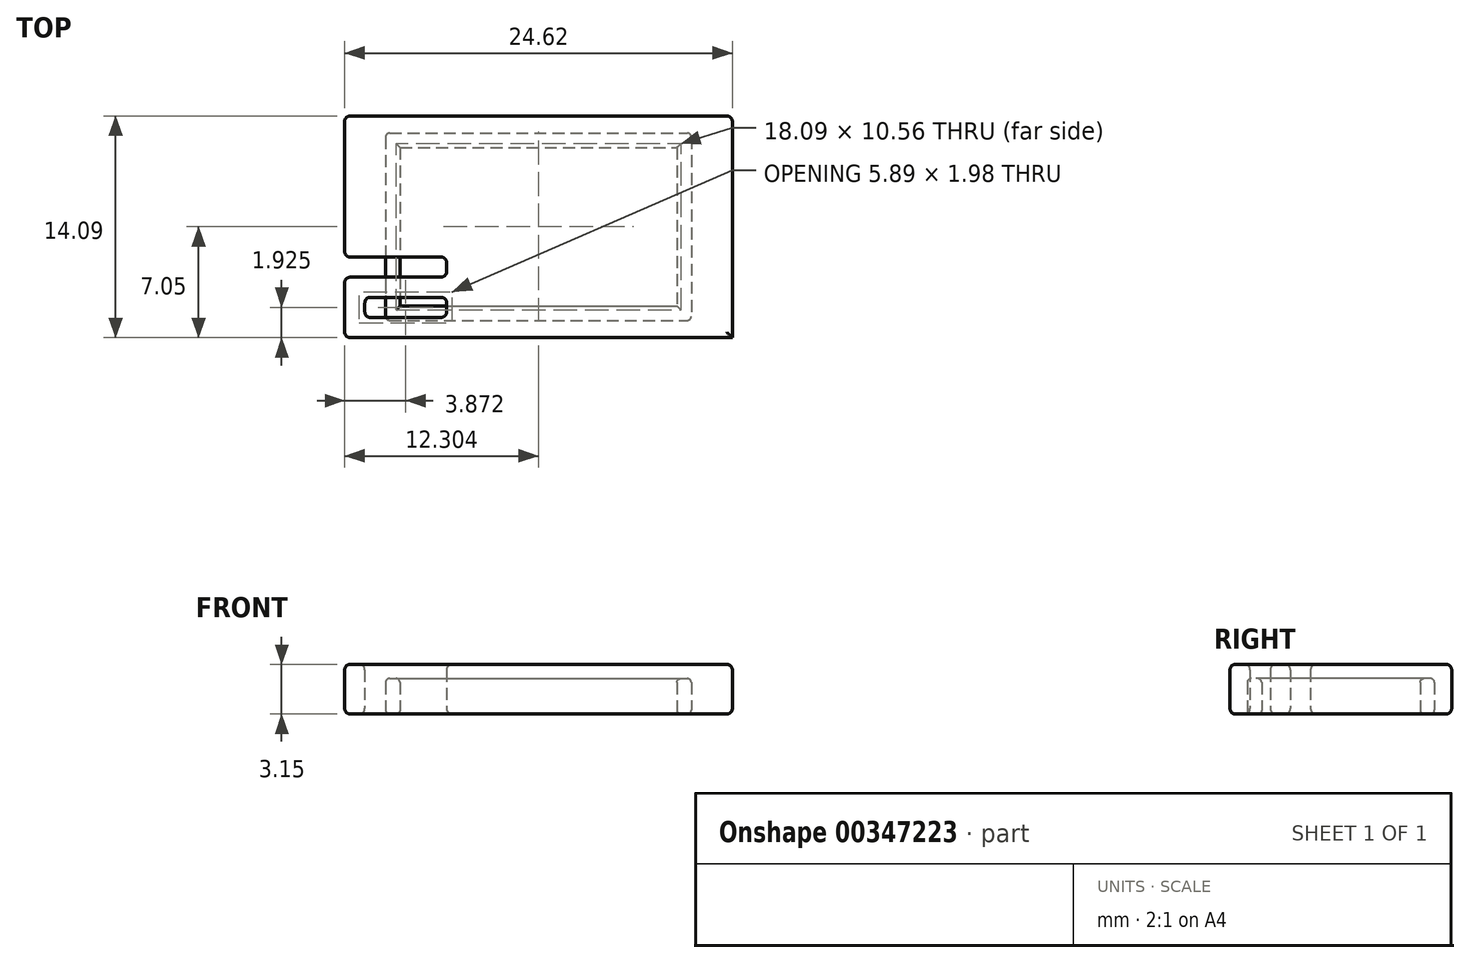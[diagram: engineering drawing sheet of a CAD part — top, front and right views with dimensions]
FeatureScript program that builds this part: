
annotation { "Feature Type Name" : "Feature", "Feature Type Description" : "" }
export const myFeature = defineFeature(function(context is Context, id is Id, definition is map)
    precondition{}
    {
        {
            var Q0;
            Q0=qCreatedBy(makeId("Top.planeOp"),FACE);
            var sketch = newSketch(context, id + "F0", { "sketchPlane" : qUnion([Q0])});
            skPoint(sketch, "E0.middle", {"position": v(0, 0) * mm});
            skLineSegment(sketch, "E1.bottom", {"start": v(-8.79, 5.02) * mm, "end": v(8.8, 5.02) * mm});
            skLineSegment(sketch, "E1.top", {"start": v(-8.79, -5.04) * mm, "end": v(-3.25, -5.04) * mm});
            skLineSegment(sketch, "E1.left", {"start": v(-8.79, 5.02) * mm, "end": v(-8.79, -5.04) * mm});
            skLineSegment(sketch, "E1.right", {"start": v(8.8, 5.02) * mm, "end": v(8.8, -5.04) * mm});
            skLineSegment(sketch, "E2", {"start": v(-8.79, 0.45) * mm, "end": v(-3.25, 0.45) * mm});
            skLineSegment(sketch, "E3", {"start": v(-3.25, 0.45) * mm, "end": v(-3.25, 1.36) * mm});
            skLineSegment(sketch, "E4", {"start": v(-3.25, 1.36) * mm, "end": v(-7.87, 1.36) * mm});
            skLineSegment(sketch, "E5", {"start": v(-3.25, 2.73) * mm, "end": v(-4.32, 2.73) * mm, "construction": true});
            skLineSegment(sketch, "E6.MirrorCS", {"start": v(-3.25, 4.1) * mm, "end": v(-7.87, 4.1) * mm});
            skLineSegment(sketch, "E7", {"start": v(-7.87, 4.1) * mm, "end": v(-7.87, 1.36) * mm});
            skLineSegment(sketch, "E8", {"start": v(-2.54, 0.45) * mm, "end": v(-2.54, 5.02) * mm});
            skLineSegment(sketch, "E9", {"start": v(-2.54, 0.45) * mm, "end": v(-1.62, 0.45) * mm});
            skLineSegment(sketch, "E10.trimOffspring", {"start": v(-3.25, 4.1) * mm, "end": v(-3.25, 5.02) * mm});
            skLineSegment(sketch, "E11", {"start": v(-1.62, 4.1) * mm, "end": v(-1.62, 0.45) * mm});
            skLineSegment(sketch, "E12", {"start": v(8.8, 0.45) * mm, "end": v(3.26, 0.45) * mm});
            skLineSegment(sketch, "E13.0", {"start": v(8.8, 1.36) * mm, "end": v(3.27, 1.36) * mm});
            skLineSegment(sketch, "E14.0", {"start": v(8.8, 2.28) * mm, "end": v(3.26, 2.28) * mm});
            skLineSegment(sketch, "E15.0", {"start": v(8.8, 3.2) * mm, "end": v(3.27, 3.2) * mm});
            skLineSegment(sketch, "E16.0", {"start": v(8.8, 4.1) * mm, "end": v(3.26, 4.1) * mm});
            skLineSegment(sketch, "E17", {"start": v(3.26, 0.45) * mm, "end": v(3.27, 1.36) * mm});
            skLineSegment(sketch, "E18", {"start": v(3.26, 2.28) * mm, "end": v(3.27, 3.2) * mm});
            skLineSegment(sketch, "E19", {"start": v(3.26, 4.1) * mm, "end": v(3.26, 5.02) * mm});
            skLineSegment(sketch, "E20", {"start": v(-1.62, 4.1) * mm, "end": v(2.5, 4.1) * mm});
            skLineSegment(sketch, "E21", {"start": v(2.5, 4.1) * mm, "end": v(2.5, 5.02) * mm});
            skLineSegment(sketch, "E22", {"start": v(-8.79, -0.47) * mm, "end": v(-3.25, -0.47) * mm});
            skLineSegment(sketch, "E23", {"start": v(3.26, -0.47) * mm, "end": v(3.26, -1.38) * mm});
            skLineSegment(sketch, "E24.0", {"start": v(-7.87, -4.13) * mm, "end": v(-4.17, -4.13) * mm});
            skLineSegment(sketch, "E25.0", {"start": v(-7.87, -3.21) * mm, "end": v(-4.17, -3.21) * mm});
            skLineSegment(sketch, "E26.0", {"start": v(-8.79, -2.3) * mm, "end": v(-4.17, -2.3) * mm});
            skLineSegment(sketch, "E27.0", {"start": v(-8.79, -1.38) * mm, "end": v(-4.17, -1.38) * mm});
            skLineSegment(sketch, "E28", {"start": v(2.5, -0.47) * mm, "end": v(2.5, -1.38) * mm});
            skLineSegment(sketch, "E29", {"start": v(-2.54, -0.47) * mm, "end": v(-2.54, -1.38) * mm});
            skLineSegment(sketch, "E30", {"start": v(-0.46, -1.38) * mm, "end": v(-0.46, -5.04) * mm});
            skLineSegment(sketch, "E31.0", {"start": v(0.45, -1.38) * mm, "end": v(0.45, -5.04) * mm});
            skLineSegment(sketch, "E32.trimOffspring", {"start": v(0.45, -1.38) * mm, "end": v(2.5, -1.38) * mm});
            skLineSegment(sketch, "E33.trimOffspring", {"start": v(3.26, -2.3) * mm, "end": v(8.8, -2.3) * mm});
            skLineSegment(sketch, "E34.trimOffspring", {"start": v(3.26, -4.13) * mm, "end": v(8.8, -4.13) * mm});
            skLineSegment(sketch, "E35", {"start": v(-3.25, -0.47) * mm, "end": v(-3.25, -5.04) * mm});
            skLineSegment(sketch, "E36", {"start": v(-4.17, -1.38) * mm, "end": v(-4.17, -2.3) * mm});
            skLineSegment(sketch, "E37", {"start": v(-4.17, -3.21) * mm, "end": v(-4.17, -4.13) * mm});
            skLineSegment(sketch, "E38", {"start": v(-7.87, -3.21) * mm, "end": v(-7.87, -4.13) * mm});
            skLineSegment(sketch, "E39.trimOffspring", {"start": v(-2.54, -1.38) * mm, "end": v(-0.46, -1.38) * mm});
            skLineSegment(sketch, "E40.0", {"start": v(-9.7, 5.93) * mm, "end": v(9.71, 5.93) * mm});
            skLineSegment(sketch, "E40.1", {"start": v(-9.7, 5.93) * mm, "end": v(-9.7, -5.95) * mm});
            skLineSegment(sketch, "E40.2", {"start": v(-9.7, -5.95) * mm, "end": v(9.71, -5.95) * mm});
            skLineSegment(sketch, "E40.3", {"start": v(9.71, 5.93) * mm, "end": v(9.71, -5.95) * mm});
            skLineSegment(sketch, "E41.trimOffspring", {"start": v(3.26, -3.21) * mm, "end": v(8.8, -3.21) * mm});
            skLineSegment(sketch, "E42.trimOffspring", {"start": v(3.26, -5.04) * mm, "end": v(8.8, -5.04) * mm});
            skLineSegment(sketch, "E43.trimOffspring", {"start": v(-0.46, -5.04) * mm, "end": v(0.45, -5.04) * mm});
            skLineSegment(sketch, "E44.trimOffspring", {"start": v(-2.54, -0.47) * mm, "end": v(2.5, -0.47) * mm});
            skLineSegment(sketch, "E45.trimOffspring", {"start": v(3.26, -0.47) * mm, "end": v(8.8, -0.47) * mm});
            skLineSegment(sketch, "E46.trimOffspring", {"start": v(3.26, -1.38) * mm, "end": v(8.8, -1.38) * mm});
            skLineSegment(sketch, "E47.trimOffspring", {"start": v(3.26, -2.3) * mm, "end": v(3.26, -3.21) * mm});
            skLineSegment(sketch, "E48.trimOffspring", {"start": v(3.26, -4.13) * mm, "end": v(3.26, -5.04) * mm});
            skLineSegment(sketch, "E49.top", {"start": v(-8.79, -5.04) * mm, "end": v(8.8, -5.04) * mm});
            skSolve(sketch);
        }
        {
            var Q0;
            {var subQ0=sQuery(id+"F0.wireOp",EDGE,"E2");Q0=makeQuery(id+"F0.imprint","IMPRINT",FACE,{"disambiguationData":[TD([[makeQuery(id+"F0.imprint","IMPRINT",EDGE,{"derivedFrom":subQ0}),1.0]])]});}
            var Q1;
            {var subQ0=sQuery(id+"F0.wireOp",EDGE,"E8");Q1=makeQuery(id+"F0.imprint","IMPRINT",FACE,{"disambiguationData":[TD([[makeQuery(id+"F0.imprint","IMPRINT",EDGE,{"derivedFrom":subQ0}),-1.0]])]});}
            var Q2;
            {var subQ3=sQuery(id+"F0.wireOp",EDGE,"E19");Q2=makeQuery(id+"F0.imprint","IMPRINT",FACE,{"disambiguationData":[TD([[makeQuery(id+"F0.imprint","IMPRINT",EDGE,{"derivedFrom":subQ3}),-1.0]])]});}
            var Q3;
            {var subQ5=sQuery(id+"F0.wireOp",EDGE,"E18");Q3=makeQuery(id+"F0.imprint","IMPRINT",FACE,{"disambiguationData":[TD([[makeQuery(id+"F0.imprint","IMPRINT",EDGE,{"derivedFrom":subQ5}),-1.0]])]});}
            var Q4;
            {var subQ0=sQuery(id+"F0.wireOp",EDGE,"E12");Q4=makeQuery(id+"F0.imprint","IMPRINT",FACE,{"disambiguationData":[TD([[makeQuery(id+"F0.imprint","IMPRINT",EDGE,{"derivedFrom":subQ0}),-1.0]])]});}
            var Q5;
            {var subQ0=sQuery(id+"F0.wireOp",EDGE,"E22");var subQ1=sQuery(id+"F0.wireOp",EDGE,"E1.right");var subQ2=makeQuery(id+"F0.imprint","INTERSECT",VERTEX,{"derivedFrom":[subQ1,subQ0]});Q5=makeQuery(id+"F0.imprint","IMPRINT",FACE,{"disambiguationData":[TD([[makeQuery(id+"F0.imprint","IMPRINT",EDGE,{"disambiguationData":[TD([[subQ2,-1.0]])],"derivedFrom":subQ1}),-1.0]])]});}
            var Q6;
            {var subQ0=sQuery(id+"F0.wireOp",EDGE,"E33.trimOffspring");var subQ1=sQuery(id+"F0.wireOp",EDGE,"E1.right");var subQ2=makeQuery(id+"F0.imprint","INTERSECT",VERTEX,{"derivedFrom":[subQ1,subQ0]});Q6=makeQuery(id+"F0.imprint","IMPRINT",FACE,{"disambiguationData":[TD([[makeQuery(id+"F0.imprint","IMPRINT",EDGE,{"disambiguationData":[TD([[subQ2,-1.0]])],"derivedFrom":subQ1}),-1.0]])]});}
            var Q7;
            {var subQ0=sQuery(id+"F0.wireOp",EDGE,"E1.right");var subQ1=sQuery(id+"F0.wireOp",EDGE,"E1.top");var subQ2=makeQuery(id+"F0.imprint","INTERSECT",VERTEX,{"derivedFrom":[subQ1,subQ0]});Q7=makeQuery(id+"F0.imprint","IMPRINT",FACE,{"disambiguationData":[TD([[makeQuery(id+"F0.imprint","IMPRINT",EDGE,{"disambiguationData":[TD([[subQ2,1.0]])],"derivedFrom":subQ1}),1.0]])]});}
            var Q8;
            {var subQ5=sQuery(id+"F0.wireOp",EDGE,"E28");Q8=makeQuery(id+"F0.imprint","IMPRINT",FACE,{"disambiguationData":[TD([[makeQuery(id+"F0.imprint","IMPRINT",EDGE,{"derivedFrom":subQ5}),-1.0]])]});}
            var Q9;
            {var subQ4=sQuery(id+"F0.wireOp",EDGE,"E30");var subQ7=sQuery(id+"F0.wireOp",EDGE,"E1.top");var subQ8=makeQuery(id+"F0.imprint","INTERSECT",VERTEX,{"derivedFrom":[subQ7,subQ4]});Q9=makeQuery(id+"F0.imprint","IMPRINT",FACE,{"disambiguationData":[TD([[makeQuery(id+"F0.imprint","IMPRINT",EDGE,{"disambiguationData":[TD([[subQ8,-1.0]])],"derivedFrom":subQ7}),1.0]])]});}
            var Q10;
            Q10=makeQuery(id+"F0.imprint","IMPRINT",FACE,{"disambiguationData":[TD([[makeQuery(id+"F0.imprint","IMPRINT",EDGE,{"derivedFrom":sQuery(id+"F0.wireOp",EDGE,"E25.0")}),1.0]])]});
            var Q11;
            {var subQ0=sQuery(id+"F0.wireOp",EDGE,"E27.0");Q11=makeQuery(id+"F0.imprint","IMPRINT",FACE,{"disambiguationData":[TD([[makeQuery(id+"F0.imprint","IMPRINT",EDGE,{"derivedFrom":subQ0}),1.0]])]});}
            var Q12;
            Q12=makeQuery(id+"F0.imprint","IMPRINT",FACE,{"disambiguationData":[TD([[makeQuery(id+"F0.imprint","IMPRINT",EDGE,{"derivedFrom":sQuery(id+"F0.wireOp",EDGE,"E23")}),1.0]])]});
            var Q13;
            {var subQ0=sQuery(id+"F0.wireOp",EDGE,"E33.trimOffspring");Q13=makeQuery(id+"F0.imprint","IMPRINT",FACE,{"disambiguationData":[TD([[makeQuery(id+"F0.imprint","IMPRINT",EDGE,{"derivedFrom":subQ0}),-1.0]])]});}
            var Q14;
            {var subQ0=sQuery(id+"F0.wireOp",EDGE,"E34.trimOffspring");Q14=makeQuery(id+"F0.imprint","IMPRINT",FACE,{"disambiguationData":[TD([[makeQuery(id+"F0.imprint","IMPRINT",EDGE,{"derivedFrom":subQ0}),-1.0]])]});}
            extrude(context, id + "F1", {"entities" : qUnion([Q0, Q1, Q2, Q3, Q4, Q5, Q6, Q7, Q8, Q9, Q10, Q11, Q12, Q13, Q14]), "depth" : 2.25 * mm});
        }
        {
            var Q0;
            Q0=makeQuery(id+"F0.imprint","IMPRINT",FACE,{"disambiguationData":[TD([[makeQuery(id+"F0.imprint","IMPRINT",EDGE,{"derivedFrom":sQuery(id+"F0.wireOp",EDGE,"E40.0")}),-1.0]])]});
            extrude(context, id + "F2", {"entities" : qUnion([Q0]), "depth" : 2.25 * mm});
        }
        {
            var Q0;
            Q0=makeQuery(id+"F2.opExtrude","CAP_FACE",FACE,{"disambiguationData":[OSD([sQuery(id+"F0.wireOp",EDGE,"E1.bottom"),sQuery(id+"F0.wireOp",EDGE,"E1.left"),sQuery(id+"F0.wireOp",EDGE,"E40.0"),sQuery(id+"F0.wireOp",EDGE,"E40.1"),sQuery(id+"F0.wireOp",EDGE,"E40.2"),sQuery(id+"F0.wireOp",EDGE,"E40.3"),sQuery(id+"F0.wireOp",EDGE,"E49.top"),sQuery(id+"F0.wireOp",EDGE,"E1.right")])],"isStart":false});
            var Q1;
            Q1=makeQuery(id+"F1.opExtrude","CAP_FACE",FACE,{"disambiguationData":[OSD([sQuery(id+"F0.wireOp",EDGE,"E1.bottom"),sQuery(id+"F0.wireOp",EDGE,"E1.left"),sQuery(id+"F0.wireOp",EDGE,"E2"),sQuery(id+"F0.wireOp",EDGE,"E3"),sQuery(id+"F0.wireOp",EDGE,"E4"),sQuery(id+"F0.wireOp",EDGE,"E6.MirrorCS"),sQuery(id+"F0.wireOp",EDGE,"E7"),sQuery(id+"F0.wireOp",EDGE,"E10.trimOffspring")])],"isStart":false});
            var Q2;
            Q2=makeQuery(id+"F1.opExtrude","CAP_FACE",FACE,{"disambiguationData":[OSD([sQuery(id+"F0.wireOp",EDGE,"E1.left"),sQuery(id+"F0.wireOp",EDGE,"E22"),sQuery(id+"F0.wireOp",EDGE,"E24.0"),sQuery(id+"F0.wireOp",EDGE,"E25.0"),sQuery(id+"F0.wireOp",EDGE,"E26.0"),sQuery(id+"F0.wireOp",EDGE,"E27.0"),sQuery(id+"F0.wireOp",EDGE,"E35"),sQuery(id+"F0.wireOp",EDGE,"E36"),sQuery(id+"F0.wireOp",EDGE,"E37"),sQuery(id+"F0.wireOp",EDGE,"E38"),sQuery(id+"F0.wireOp",EDGE,"E49.top")])],"isStart":false});
            var Q3;
            Q3=makeQuery(id+"F1.opExtrude","CAP_FACE",FACE,{"disambiguationData":[OSD([sQuery(id+"F0.wireOp",EDGE,"E28"),sQuery(id+"F0.wireOp",EDGE,"E29"),sQuery(id+"F0.wireOp",EDGE,"E30"),sQuery(id+"F0.wireOp",EDGE,"E31.0"),sQuery(id+"F0.wireOp",EDGE,"E32.trimOffspring"),sQuery(id+"F0.wireOp",EDGE,"E39.trimOffspring"),sQuery(id+"F0.wireOp",EDGE,"E44.trimOffspring"),sQuery(id+"F0.wireOp",EDGE,"E49.top")])],"isStart":false});
            var Q4;
            Q4=makeQuery(id+"F1.opExtrude","CAP_FACE",FACE,{"disambiguationData":[OSD([sQuery(id+"F0.wireOp",EDGE,"E1.bottom"),sQuery(id+"F0.wireOp",EDGE,"E8"),sQuery(id+"F0.wireOp",EDGE,"E9"),sQuery(id+"F0.wireOp",EDGE,"E11"),sQuery(id+"F0.wireOp",EDGE,"E20"),sQuery(id+"F0.wireOp",EDGE,"E21")])],"isStart":false});
            var Q5;
            Q5=makeQuery(id+"F1.opExtrude","CAP_FACE",FACE,{"disambiguationData":[OSD([sQuery(id+"F0.wireOp",EDGE,"E12"),sQuery(id+"F0.wireOp",EDGE,"E13.0"),sQuery(id+"F0.wireOp",EDGE,"E17"),sQuery(id+"F0.wireOp",EDGE,"E1.right")])],"isStart":false});
            var Q6;
            Q6=makeQuery(id+"F1.opExtrude","CAP_FACE",FACE,{"disambiguationData":[OSD([sQuery(id+"F0.wireOp",EDGE,"E14.0"),sQuery(id+"F0.wireOp",EDGE,"E15.0"),sQuery(id+"F0.wireOp",EDGE,"E18"),sQuery(id+"F0.wireOp",EDGE,"E1.right")])],"isStart":false});
            var Q7;
            Q7=makeQuery(id+"F1.opExtrude","CAP_FACE",FACE,{"disambiguationData":[OSD([sQuery(id+"F0.wireOp",EDGE,"E1.bottom"),sQuery(id+"F0.wireOp",EDGE,"E16.0"),sQuery(id+"F0.wireOp",EDGE,"E19"),sQuery(id+"F0.wireOp",EDGE,"E1.right")])],"isStart":false});
            var Q8;
            Q8=makeQuery(id+"F1.opExtrude","CAP_FACE",FACE,{"disambiguationData":[OSD([sQuery(id+"F0.wireOp",EDGE,"E23"),sQuery(id+"F0.wireOp",EDGE,"E45.trimOffspring"),sQuery(id+"F0.wireOp",EDGE,"E46.trimOffspring"),sQuery(id+"F0.wireOp",EDGE,"E1.right")])],"isStart":false});
            var Q9;
            Q9=makeQuery(id+"F1.opExtrude","CAP_FACE",FACE,{"disambiguationData":[OSD([sQuery(id+"F0.wireOp",EDGE,"E33.trimOffspring"),sQuery(id+"F0.wireOp",EDGE,"E41.trimOffspring"),sQuery(id+"F0.wireOp",EDGE,"E47.trimOffspring"),sQuery(id+"F0.wireOp",EDGE,"E1.right")])],"isStart":false});
            var Q10;
            Q10=makeQuery(id+"F1.opExtrude","CAP_FACE",FACE,{"disambiguationData":[OSD([sQuery(id+"F0.wireOp",EDGE,"E34.trimOffspring"),sQuery(id+"F0.wireOp",EDGE,"E48.trimOffspring"),sQuery(id+"F0.wireOp",EDGE,"E49.top"),sQuery(id+"F0.wireOp",EDGE,"E1.right")])],"isStart":false});
            var Q11;
            Q11=makeQuery(id+"F1.opExtrude","CAP_FACE",FACE,{"disambiguationData":[OSD([sQuery(id+"F0.wireOp",EDGE,"E1.bottom"),sQuery(id+"F0.wireOp",EDGE,"E1.left"),sQuery(id+"F0.wireOp",EDGE,"E2"),sQuery(id+"F0.wireOp",EDGE,"E3"),sQuery(id+"F0.wireOp",EDGE,"E4"),sQuery(id+"F0.wireOp",EDGE,"E6.MirrorCS"),sQuery(id+"F0.wireOp",EDGE,"E7"),sQuery(id+"F0.wireOp",EDGE,"E10.trimOffspring")])],"isStart":true});
            var Q12;
            Q12=makeQuery(id+"F1.opExtrude","CAP_FACE",FACE,{"disambiguationData":[OSD([sQuery(id+"F0.wireOp",EDGE,"E1.left"),sQuery(id+"F0.wireOp",EDGE,"E22"),sQuery(id+"F0.wireOp",EDGE,"E24.0"),sQuery(id+"F0.wireOp",EDGE,"E25.0"),sQuery(id+"F0.wireOp",EDGE,"E26.0"),sQuery(id+"F0.wireOp",EDGE,"E27.0"),sQuery(id+"F0.wireOp",EDGE,"E35"),sQuery(id+"F0.wireOp",EDGE,"E36"),sQuery(id+"F0.wireOp",EDGE,"E37"),sQuery(id+"F0.wireOp",EDGE,"E38"),sQuery(id+"F0.wireOp",EDGE,"E49.top")])],"isStart":true});
            var Q13;
            Q13=makeQuery(id+"F1.opExtrude","CAP_FACE",FACE,{"disambiguationData":[OSD([sQuery(id+"F0.wireOp",EDGE,"E28"),sQuery(id+"F0.wireOp",EDGE,"E29"),sQuery(id+"F0.wireOp",EDGE,"E30"),sQuery(id+"F0.wireOp",EDGE,"E31.0"),sQuery(id+"F0.wireOp",EDGE,"E32.trimOffspring"),sQuery(id+"F0.wireOp",EDGE,"E39.trimOffspring"),sQuery(id+"F0.wireOp",EDGE,"E44.trimOffspring"),sQuery(id+"F0.wireOp",EDGE,"E49.top")])],"isStart":true});
            var Q14;
            Q14=makeQuery(id+"F1.opExtrude","CAP_FACE",FACE,{"disambiguationData":[OSD([sQuery(id+"F0.wireOp",EDGE,"E1.bottom"),sQuery(id+"F0.wireOp",EDGE,"E8"),sQuery(id+"F0.wireOp",EDGE,"E9"),sQuery(id+"F0.wireOp",EDGE,"E11"),sQuery(id+"F0.wireOp",EDGE,"E20"),sQuery(id+"F0.wireOp",EDGE,"E21")])],"isStart":true});
            var Q15;
            Q15=makeQuery(id+"F1.opExtrude","CAP_FACE",FACE,{"disambiguationData":[OSD([sQuery(id+"F0.wireOp",EDGE,"E34.trimOffspring"),sQuery(id+"F0.wireOp",EDGE,"E48.trimOffspring"),sQuery(id+"F0.wireOp",EDGE,"E49.top"),sQuery(id+"F0.wireOp",EDGE,"E1.right")])],"isStart":true});
            var Q16;
            Q16=makeQuery(id+"F1.opExtrude","CAP_FACE",FACE,{"disambiguationData":[OSD([sQuery(id+"F0.wireOp",EDGE,"E33.trimOffspring"),sQuery(id+"F0.wireOp",EDGE,"E41.trimOffspring"),sQuery(id+"F0.wireOp",EDGE,"E47.trimOffspring"),sQuery(id+"F0.wireOp",EDGE,"E1.right")])],"isStart":true});
            var Q17;
            Q17=makeQuery(id+"F1.opExtrude","CAP_FACE",FACE,{"disambiguationData":[OSD([sQuery(id+"F0.wireOp",EDGE,"E23"),sQuery(id+"F0.wireOp",EDGE,"E45.trimOffspring"),sQuery(id+"F0.wireOp",EDGE,"E46.trimOffspring"),sQuery(id+"F0.wireOp",EDGE,"E1.right")])],"isStart":true});
            var Q18;
            Q18=makeQuery(id+"F1.opExtrude","CAP_FACE",FACE,{"disambiguationData":[OSD([sQuery(id+"F0.wireOp",EDGE,"E12"),sQuery(id+"F0.wireOp",EDGE,"E13.0"),sQuery(id+"F0.wireOp",EDGE,"E17"),sQuery(id+"F0.wireOp",EDGE,"E1.right")])],"isStart":true});
            var Q19;
            Q19=makeQuery(id+"F1.opExtrude","CAP_FACE",FACE,{"disambiguationData":[OSD([sQuery(id+"F0.wireOp",EDGE,"E14.0"),sQuery(id+"F0.wireOp",EDGE,"E15.0"),sQuery(id+"F0.wireOp",EDGE,"E18"),sQuery(id+"F0.wireOp",EDGE,"E1.right")])],"isStart":true});
            var Q20;
            Q20=makeQuery(id+"F1.opExtrude","CAP_FACE",FACE,{"disambiguationData":[OSD([sQuery(id+"F0.wireOp",EDGE,"E1.bottom"),sQuery(id+"F0.wireOp",EDGE,"E16.0"),sQuery(id+"F0.wireOp",EDGE,"E19"),sQuery(id+"F0.wireOp",EDGE,"E1.right")])],"isStart":true});
            var Q21;
            Q21=makeQuery(id+"F2.opExtrude","CAP_FACE",FACE,{"disambiguationData":[OSD([sQuery(id+"F0.wireOp",EDGE,"E1.bottom"),sQuery(id+"F0.wireOp",EDGE,"E1.left"),sQuery(id+"F0.wireOp",EDGE,"E40.0"),sQuery(id+"F0.wireOp",EDGE,"E40.1"),sQuery(id+"F0.wireOp",EDGE,"E40.2"),sQuery(id+"F0.wireOp",EDGE,"E40.3"),sQuery(id+"F0.wireOp",EDGE,"E49.top"),sQuery(id+"F0.wireOp",EDGE,"E1.right")])],"isStart":true});
            var Q22;
            Q22=makeQuery(id+"F2.opExtrude","SWEPT_EDGE",EDGE,{"disambiguationData":[OSD([sQuery(id+"F0.wireOp",EDGE,"E40.2"),sQuery(id+"F0.wireOp",EDGE,"E40.3")])]});
            var Q23;
            Q23=makeQuery(id+"F2.opExtrude","SWEPT_EDGE",EDGE,{"disambiguationData":[OSD([sQuery(id+"F0.wireOp",EDGE,"E40.0"),sQuery(id+"F0.wireOp",EDGE,"E40.3")])]});
            var Q24;
            Q24=makeQuery(id+"F2.opExtrude","SWEPT_EDGE",EDGE,{"disambiguationData":[OSD([sQuery(id+"F0.wireOp",EDGE,"E40.0"),sQuery(id+"F0.wireOp",EDGE,"E40.1")])]});
            var Q25;
            Q25=makeQuery(id+"F2.opExtrude","SWEPT_EDGE",EDGE,{"disambiguationData":[OSD([sQuery(id+"F0.wireOp",EDGE,"E40.1"),sQuery(id+"F0.wireOp",EDGE,"E40.2")])]});
            var Q26;
            Q26=makeQuery(id+"F1.opExtrude","SWEPT_EDGE",EDGE,{"disambiguationData":[OSD([sQuery(id+"F0.wireOp",EDGE,"E2"),sQuery(id+"F0.wireOp",EDGE,"E3")])]});
            var Q27;
            Q27=makeQuery(id+"F1.opExtrude","SWEPT_EDGE",EDGE,{"disambiguationData":[OSD([sQuery(id+"F0.wireOp",EDGE,"E8"),sQuery(id+"F0.wireOp",EDGE,"E9")])]});
            var Q28;
            Q28=makeQuery(id+"F1.opExtrude","SWEPT_EDGE",EDGE,{"disambiguationData":[OSD([sQuery(id+"F0.wireOp",EDGE,"E9"),sQuery(id+"F0.wireOp",EDGE,"E11")])]});
            var Q29;
            Q29=makeQuery(id+"F1.opExtrude","SWEPT_EDGE",EDGE,{"disambiguationData":[OSD([sQuery(id+"F0.wireOp",EDGE,"E3"),sQuery(id+"F0.wireOp",EDGE,"E4")])]});
            var Q30;
            Q30=makeQuery(id+"F1.opExtrude","SWEPT_EDGE",EDGE,{"disambiguationData":[OSD([sQuery(id+"F0.wireOp",EDGE,"E6.MirrorCS"),sQuery(id+"F0.wireOp",EDGE,"E10.trimOffspring")])]});
            var Q31;
            Q31=makeQuery(id+"F1.opExtrude","SWEPT_EDGE",EDGE,{"disambiguationData":[OSD([sQuery(id+"F0.wireOp",EDGE,"E1.bottom"),sQuery(id+"F0.wireOp",EDGE,"E10.trimOffspring")])]});
            var Q32;
            Q32=makeQuery(id+"F1.opExtrude","SWEPT_EDGE",EDGE,{"disambiguationData":[OSD([sQuery(id+"F0.wireOp",EDGE,"E1.bottom"),sQuery(id+"F0.wireOp",EDGE,"E21")])]});
            var Q33;
            Q33=makeQuery(id+"F1.opExtrude","SWEPT_EDGE",EDGE,{"disambiguationData":[OSD([sQuery(id+"F0.wireOp",EDGE,"E20"),sQuery(id+"F0.wireOp",EDGE,"E21")])]});
            var Q34;
            Q34=makeQuery(id+"F1.opExtrude","SWEPT_EDGE",EDGE,{"disambiguationData":[OSD([sQuery(id+"F0.wireOp",EDGE,"E22"),sQuery(id+"F0.wireOp",EDGE,"E35")])]});
            var Q35;
            Q35=makeQuery(id+"F1.opExtrude","SWEPT_EDGE",EDGE,{"disambiguationData":[OSD([sQuery(id+"F0.wireOp",EDGE,"E28"),sQuery(id+"F0.wireOp",EDGE,"E32.trimOffspring")])]});
            var Q36;
            Q36=makeQuery(id+"F1.opExtrude","SWEPT_EDGE",EDGE,{"disambiguationData":[OSD([sQuery(id+"F0.wireOp",EDGE,"E28"),sQuery(id+"F0.wireOp",EDGE,"E44.trimOffspring")])]});
            var Q37;
            Q37=makeQuery(id+"F1.opExtrude","SWEPT_EDGE",EDGE,{"disambiguationData":[OSD([sQuery(id+"F0.wireOp",EDGE,"E29"),sQuery(id+"F0.wireOp",EDGE,"E39.trimOffspring")])]});
            var Q38;
            Q38=makeQuery(id+"F1.opExtrude","SWEPT_EDGE",EDGE,{"disambiguationData":[OSD([sQuery(id+"F0.wireOp",EDGE,"E29"),sQuery(id+"F0.wireOp",EDGE,"E44.trimOffspring")])]});
            var Q39;
            Q39=makeQuery(id+"F1.opExtrude","SWEPT_EDGE",EDGE,{"disambiguationData":[OSD([sQuery(id+"F0.wireOp",EDGE,"E1.bottom"),sQuery(id+"F0.wireOp",EDGE,"E8")])]});
            var Q40;
            Q40=makeQuery(id+"F1.opExtrude","SWEPT_EDGE",EDGE,{"disambiguationData":[OSD([sQuery(id+"F0.wireOp",EDGE,"E14.0"),sQuery(id+"F0.wireOp",EDGE,"E18")])]});
            var Q41;
            Q41=makeQuery(id+"F1.opExtrude","SWEPT_EDGE",EDGE,{"disambiguationData":[OSD([sQuery(id+"F0.wireOp",EDGE,"E15.0"),sQuery(id+"F0.wireOp",EDGE,"E18")])]});
            var Q42;
            Q42=makeQuery(id+"F1.opExtrude","SWEPT_EDGE",EDGE,{"disambiguationData":[OSD([sQuery(id+"F0.wireOp",EDGE,"E16.0"),sQuery(id+"F0.wireOp",EDGE,"E19")])]});
            var Q43;
            Q43=makeQuery(id+"F1.opExtrude","SWEPT_EDGE",EDGE,{"disambiguationData":[OSD([sQuery(id+"F0.wireOp",EDGE,"E16.0"),sQuery(id+"F0.wireOp",EDGE,"E1.right")])]});
            var Q44;
            Q44=makeQuery(id+"F1.opExtrude","SWEPT_EDGE",EDGE,{"disambiguationData":[OSD([sQuery(id+"F0.wireOp",EDGE,"E1.bottom"),sQuery(id+"F0.wireOp",EDGE,"E19")])]});
            var Q45;
            Q45=makeQuery(id+"F1.opExtrude","SWEPT_EDGE",EDGE,{"disambiguationData":[OSD([sQuery(id+"F0.wireOp",EDGE,"E14.0"),sQuery(id+"F0.wireOp",EDGE,"E1.right")])]});
            var Q46;
            Q46=makeQuery(id+"F1.opExtrude","SWEPT_EDGE",EDGE,{"disambiguationData":[OSD([sQuery(id+"F0.wireOp",EDGE,"E12"),sQuery(id+"F0.wireOp",EDGE,"E17")])]});
            var Q47;
            Q47=makeQuery(id+"F1.opExtrude","SWEPT_EDGE",EDGE,{"disambiguationData":[OSD([sQuery(id+"F0.wireOp",EDGE,"E13.0"),sQuery(id+"F0.wireOp",EDGE,"E17")])]});
            var Q48;
            Q48=makeQuery(id+"F1.opExtrude","SWEPT_EDGE",EDGE,{"disambiguationData":[OSD([sQuery(id+"F0.wireOp",EDGE,"E12"),sQuery(id+"F0.wireOp",EDGE,"E1.right")])]});
            var Q49;
            Q49=makeQuery(id+"F1.opExtrude","SWEPT_EDGE",EDGE,{"disambiguationData":[OSD([sQuery(id+"F0.wireOp",EDGE,"E23"),sQuery(id+"F0.wireOp",EDGE,"E46.trimOffspring")])]});
            var Q50;
            Q50=makeQuery(id+"F1.opExtrude","SWEPT_EDGE",EDGE,{"disambiguationData":[OSD([sQuery(id+"F0.wireOp",EDGE,"E23"),sQuery(id+"F0.wireOp",EDGE,"E45.trimOffspring")])]});
            var Q51;
            Q51=makeQuery(id+"F1.opExtrude","SWEPT_EDGE",EDGE,{"disambiguationData":[OSD([sQuery(id+"F0.wireOp",EDGE,"E46.trimOffspring"),sQuery(id+"F0.wireOp",EDGE,"E1.right")])]});
            var Q52;
            Q52=makeQuery(id+"F1.opExtrude","SWEPT_EDGE",EDGE,{"disambiguationData":[OSD([sQuery(id+"F0.wireOp",EDGE,"E45.trimOffspring"),sQuery(id+"F0.wireOp",EDGE,"E1.right")])]});
            var Q53;
            Q53=makeQuery(id+"F1.opExtrude","SWEPT_EDGE",EDGE,{"disambiguationData":[OSD([sQuery(id+"F0.wireOp",EDGE,"E13.0"),sQuery(id+"F0.wireOp",EDGE,"E1.right")])]});
            var Q54;
            Q54=makeQuery(id+"F1.opExtrude","SWEPT_EDGE",EDGE,{"disambiguationData":[OSD([sQuery(id+"F0.wireOp",EDGE,"E15.0"),sQuery(id+"F0.wireOp",EDGE,"E1.right")])]});
            var Q55;
            Q55=makeQuery(id+"F1.opExtrude","SWEPT_EDGE",EDGE,{"disambiguationData":[OSD([sQuery(id+"F0.wireOp",EDGE,"E34.trimOffspring"),sQuery(id+"F0.wireOp",EDGE,"E48.trimOffspring")])]});
            var Q56;
            Q56=makeQuery(id+"F1.opExtrude","SWEPT_EDGE",EDGE,{"disambiguationData":[OSD([sQuery(id+"F0.wireOp",EDGE,"E48.trimOffspring"),sQuery(id+"F0.wireOp",EDGE,"E49.top")])]});
            var Q57;
            Q57=makeQuery(id+"F1.opExtrude","SWEPT_EDGE",EDGE,{"disambiguationData":[OSD([sQuery(id+"F0.wireOp",EDGE,"E34.trimOffspring"),sQuery(id+"F0.wireOp",EDGE,"E1.right")])]});
            var Q58;
            Q58=makeQuery(id+"F1.opExtrude","SWEPT_EDGE",EDGE,{"disambiguationData":[OSD([sQuery(id+"F0.wireOp",EDGE,"E33.trimOffspring"),sQuery(id+"F0.wireOp",EDGE,"E1.right")])]});
            var Q59;
            Q59=makeQuery(id+"F1.opExtrude","SWEPT_EDGE",EDGE,{"disambiguationData":[OSD([sQuery(id+"F0.wireOp",EDGE,"E33.trimOffspring"),sQuery(id+"F0.wireOp",EDGE,"E47.trimOffspring")])]});
            var Q60;
            Q60=makeQuery(id+"F1.opExtrude","SWEPT_EDGE",EDGE,{"disambiguationData":[OSD([sQuery(id+"F0.wireOp",EDGE,"E41.trimOffspring"),sQuery(id+"F0.wireOp",EDGE,"E47.trimOffspring")])]});
            var Q61;
            Q61=makeQuery(id+"F1.opExtrude","SWEPT_EDGE",EDGE,{"disambiguationData":[OSD([sQuery(id+"F0.wireOp",EDGE,"E41.trimOffspring"),sQuery(id+"F0.wireOp",EDGE,"E1.right")])]});
            var Q62;
            Q62=makeQuery(id+"F1.opExtrude","SWEPT_EDGE",EDGE,{"disambiguationData":[OSD([sQuery(id+"F0.wireOp",EDGE,"E1.left"),sQuery(id+"F0.wireOp",EDGE,"E2")])]});
            var Q63;
            Q63=makeQuery(id+"F1.opExtrude","SWEPT_EDGE",EDGE,{"disambiguationData":[OSD([sQuery(id+"F0.wireOp",EDGE,"E1.left"),sQuery(id+"F0.wireOp",EDGE,"E27.0")])]});
            var Q64;
            Q64=makeQuery(id+"F1.opExtrude","SWEPT_EDGE",EDGE,{"disambiguationData":[OSD([sQuery(id+"F0.wireOp",EDGE,"E25.0"),sQuery(id+"F0.wireOp",EDGE,"E38")])]});
            var Q65;
            Q65=makeQuery(id+"F1.opExtrude","SWEPT_EDGE",EDGE,{"disambiguationData":[OSD([sQuery(id+"F0.wireOp",EDGE,"E25.0"),sQuery(id+"F0.wireOp",EDGE,"E37")])]});
            var Q66;
            Q66=makeQuery(id+"F1.opExtrude","SWEPT_EDGE",EDGE,{"disambiguationData":[OSD([sQuery(id+"F0.wireOp",EDGE,"E24.0"),sQuery(id+"F0.wireOp",EDGE,"E38")])]});
            var Q67;
            Q67=makeQuery(id+"F1.opExtrude","SWEPT_EDGE",EDGE,{"disambiguationData":[OSD([sQuery(id+"F0.wireOp",EDGE,"E24.0"),sQuery(id+"F0.wireOp",EDGE,"E37")])]});
            var Q68;
            Q68=makeQuery(id+"F1.opExtrude","SWEPT_EDGE",EDGE,{"disambiguationData":[OSD([sQuery(id+"F0.wireOp",EDGE,"E26.0"),sQuery(id+"F0.wireOp",EDGE,"E36")])]});
            var Q69;
            Q69=makeQuery(id+"F1.opExtrude","SWEPT_EDGE",EDGE,{"disambiguationData":[OSD([sQuery(id+"F0.wireOp",EDGE,"E27.0"),sQuery(id+"F0.wireOp",EDGE,"E36")])]});
            var Q70;
            Q70=makeQuery(id+"F1.opExtrude","SWEPT_EDGE",EDGE,{"disambiguationData":[OSD([sQuery(id+"F0.wireOp",EDGE,"E1.left"),sQuery(id+"F0.wireOp",EDGE,"E26.0")])]});
            var Q71;
            Q71=makeQuery(id+"F1.opExtrude","SWEPT_EDGE",EDGE,{"disambiguationData":[OSD([sQuery(id+"F0.wireOp",EDGE,"E35"),sQuery(id+"F0.wireOp",EDGE,"E49.top")])]});
            var Q72;
            Q72=makeQuery(id+"F1.opExtrude","SWEPT_EDGE",EDGE,{"disambiguationData":[OSD([sQuery(id+"F0.wireOp",EDGE,"E4"),sQuery(id+"F0.wireOp",EDGE,"E7")])]});
            var Q73;
            Q73=makeQuery(id+"F1.opExtrude","SWEPT_EDGE",EDGE,{"disambiguationData":[OSD([sQuery(id+"F0.wireOp",EDGE,"E6.MirrorCS"),sQuery(id+"F0.wireOp",EDGE,"E7")])]});
            var Q74;
            Q74=makeQuery(id+"F1.opExtrude","SWEPT_EDGE",EDGE,{"disambiguationData":[OSD([sQuery(id+"F0.wireOp",EDGE,"E11"),sQuery(id+"F0.wireOp",EDGE,"E20")])]});
            var Q75;
            Q75=makeQuery(id+"F1.opExtrude","SWEPT_EDGE",EDGE,{"disambiguationData":[OSD([sQuery(id+"F0.wireOp",EDGE,"E31.0"),sQuery(id+"F0.wireOp",EDGE,"E32.trimOffspring")])]});
            var Q76;
            Q76=makeQuery(id+"F1.opExtrude","SWEPT_EDGE",EDGE,{"disambiguationData":[OSD([sQuery(id+"F0.wireOp",EDGE,"E30"),sQuery(id+"F0.wireOp",EDGE,"E39.trimOffspring")])]});
            var Q77;
            Q77=makeQuery(id+"F1.opExtrude","SWEPT_EDGE",EDGE,{"disambiguationData":[OSD([sQuery(id+"F0.wireOp",EDGE,"E1.left"),sQuery(id+"F0.wireOp",EDGE,"E22")])]});
            var Q78;
            Q78=makeQuery(id+"F1.opExtrude","SWEPT_EDGE",EDGE,{"disambiguationData":[OSD([sQuery(id+"F0.wireOp",EDGE,"E31.0"),sQuery(id+"F0.wireOp",EDGE,"E49.top")])]});
            var Q79;
            Q79=makeQuery(id+"F1.opExtrude","SWEPT_EDGE",EDGE,{"disambiguationData":[OSD([sQuery(id+"F0.wireOp",EDGE,"E30"),sQuery(id+"F0.wireOp",EDGE,"E49.top")])]});
            fillet(context, id + "F3", {"entities" : qUnion([Q0, Q1, Q2, Q3, Q4, Q5, Q6, Q7, Q8, Q9, Q10, Q11, Q12, Q13, Q14, Q15, Q16, Q17, Q18, Q19, Q20, Q21, Q22, Q23, Q24, Q25, Q26, Q27, Q28, Q29, Q30, Q31, Q32, Q33, Q34, Q35, Q36, Q37, Q38, Q39, Q40, Q41, Q42, Q43, Q44, Q45, Q46, Q47, Q48, Q49, Q50, Q51, Q52, Q53, Q54, Q55, Q56, Q57, Q58, Q59, Q60, Q61, Q62, Q63, Q64, Q65, Q66, Q67, Q68, Q69, Q70, Q71, Q72, Q73, Q74, Q75, Q76, Q77, Q78, Q79]), "radius" : .25 * mm, "tangentPropagation" : true, "allowEdgeOverflow" : false});
        }
        {
            var Q0;
            Q0=makeQuery(id+"F1.opExtrude","SWEPT_BODY",BODY,{"disambiguationData":[OSD([sQuery(id+"F0.wireOp",EDGE,"E34.trimOffspring"),sQuery(id+"F0.wireOp",EDGE,"E48.trimOffspring"),sQuery(id+"F0.wireOp",EDGE,"E49.top"),sQuery(id+"F0.wireOp",EDGE,"E1.right")])]});
            var Q1;
            Q1=qCreatedBy(makeId("Origin.pointOp"),VERTEX);
            transform(context, id + "F4", {"entities" : qUnion([Q0]), "transformType" : TransformType.SCALE_UNIFORMLY, "scale" : 1.4, "scalePoint" : qUnion([Q1]), "makeCopy" : false});
        }
    });
